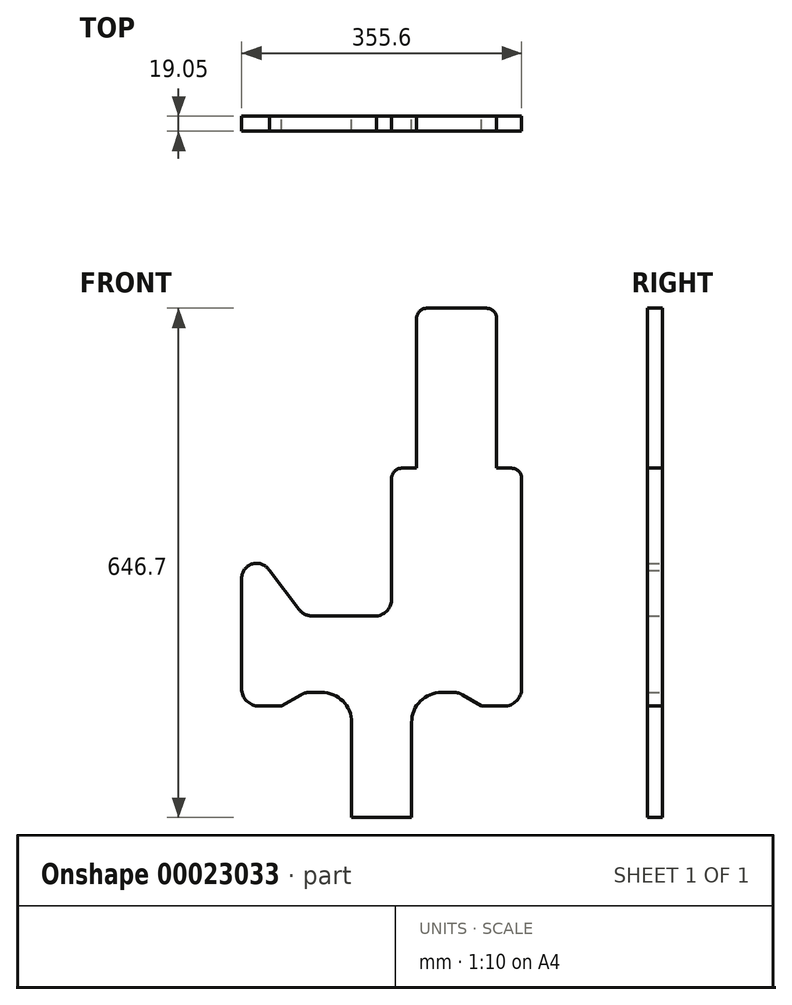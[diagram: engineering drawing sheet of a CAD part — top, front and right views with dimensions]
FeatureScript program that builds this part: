
annotation { "Feature Type Name" : "Feature", "Feature Type Description" : "" }
export const myFeature = defineFeature(function(context is Context, id is Id, definition is map)
    precondition{}
    {
        {
            var Q0;
            Q0=qCreatedBy(makeId("Front.planeOp"),FACE);
            var sketch = newSketch(context, id + "F0", { "sketchPlane" : qUnion([Q0])});
            skLineSegment(sketch, "E0", {"start": v(165.1, -62.38) * mm, "end": v(165.1, 204.91) * mm});
            skLineSegment(sketch, "E1", {"start": v(152.4, 217.61) * mm, "end": v(133.35, 217.61) * mm});
            skLineSegment(sketch, "E2", {"start": v(133.35, 217.61) * mm, "end": v(133.35, 408.11) * mm});
            skLineSegment(sketch, "E3", {"start": v(120.65, 420.81) * mm, "end": v(44.45, 420.81) * mm});
            skLineSegment(sketch, "E4", {"start": v(31.75, 408.11) * mm, "end": v(31.75, 217.61) * mm});
            skLineSegment(sketch, "E5", {"start": v(31.75, 217.61) * mm, "end": v(23.4, 217.61) * mm});
            skLineSegment(sketch, "E6", {"start": v(-190.5, -62.38) * mm, "end": v(-190.5, 29.7) * mm});
            skArc(sketch, "E7.filletArc", {"start": v(133.35, 408.11) * mm, "mid": v(129.63, 417.1) * mm, "end": v(120.65, 420.81) * mm});
            skArc(sketch, "E8.filletArc", {"start": v(44.45, 420.81) * mm, "mid": v(35.47, 417.1) * mm, "end": v(31.75, 408.11) * mm});
            skArc(sketch, "E9.filletArc", {"start": v(165.1, 204.91) * mm, "mid": v(161.38, 213.9) * mm, "end": v(152.4, 217.61) * mm});
            skLineSegment(sketch, "E10", {"start": v(31.75, 217.61) * mm, "end": v(12.7, 217.61) * mm});
            skLineSegment(sketch, "E11", {"start": v(0, 204.91) * mm, "end": v(0, 51.68) * mm});
            skArc(sketch, "E12.filletArc", {"start": v(12.7, 217.61) * mm, "mid": v(3.72, 213.9) * mm, "end": v(0, 204.91) * mm});
            skArc(sketch, "E13.filletArc", {"start": v(142.88, -84.6) * mm, "mid": v(158.6, -78.1) * mm, "end": v(165.1, -62.38) * mm});
            skArc(sketch, "E14.filletArc", {"start": v(-190.5, -62.38) * mm, "mid": v(-184, -78.1) * mm, "end": v(-168.28, -84.6) * mm});
            skLineSegment(sketch, "E15", {"start": v(-100.1, 29.7) * mm, "end": v(-19, 29.7) * mm});
            skLineSegment(sketch, "E16", {"start": v(-190.5, 29.7) * mm, "end": v(-190.5, 77.85) * mm});
            skArc(sketch, "E17.filletArc", {"start": v(-19, 29.7) * mm, "mid": v(-5.4, 37.16) * mm, "end": v(0, 51.68) * mm});
            skArc(sketch, "E18", {"start": v(-155.17, 87.73) * mm, "mid": v(-176.58, 96.2) * mm, "end": v(-190.5, 77.85) * mm});
            skLineSegment(sketch, "E19", {"start": v(-155.17, 87.73) * mm, "end": v(-117.8, 38.48) * mm});
            skArc(sketch, "E20.filletArc", {"start": v(-117.8, 38.48) * mm, "mid": v(-109.98, 32.01) * mm, "end": v(-100.1, 29.7) * mm});
            skLineSegment(sketch, "E21", {"start": v(142.88, -84.6) * mm, "end": v(114.3, -84.6) * mm});
            skLineSegment(sketch, "E22", {"start": v(-168.28, -84.6) * mm, "end": v(-139.7, -84.6) * mm});
            skLineSegment(sketch, "E23", {"start": v(-139.7, -84.6) * mm, "end": v(-115.4, -70.24) * mm});
            skLineSegment(sketch, "E24", {"start": v(90, -70.24) * mm, "end": v(114.3, -84.6) * mm});
            skArc(sketch, "E25.filletArc", {"start": v(-104.1, -67.14) * mm, "mid": v(-109.96, -67.93) * mm, "end": v(-115.4, -70.24) * mm});
            skArc(sketch, "E26.filletArc", {"start": v(90, -70.24) * mm, "mid": v(84.56, -67.93) * mm, "end": v(78.7, -67.14) * mm});
            skLineSegment(sketch, "E27", {"start": v(-12.7, -225.9) * mm, "end": v(25.4, -225.9) * mm});
            skLineSegment(sketch, "E28", {"start": v(-12.7, -225.9) * mm, "end": v(-50.8, -225.9) * mm});
            skLineSegment(sketch, "E29", {"start": v(25.4, -225.9) * mm, "end": v(25.4, -105.24) * mm});
            skLineSegment(sketch, "E30", {"start": v(-50.8, -225.9) * mm, "end": v(-50.8, -105.24) * mm});
            skLineSegment(sketch, "E31", {"start": v(-104.1, -67.14) * mm, "end": v(-88.9, -67.14) * mm});
            skLineSegment(sketch, "E32", {"start": v(63.5, -67.14) * mm, "end": v(78.7, -67.14) * mm});
            skArc(sketch, "E33.filletArc", {"start": v(-50.8, -105.24) * mm, "mid": v(-61.96, -78.3) * mm, "end": v(-88.9, -67.14) * mm});
            skArc(sketch, "E34.filletArc", {"start": v(63.5, -67.14) * mm, "mid": v(36.56, -78.3) * mm, "end": v(25.4, -105.24) * mm});
            skSolve(sketch);
        }
        {
            var Q0;
            Q0=makeQuery(id+"F0.imprint","IMPRINT",FACE,{"disambiguationData":[TD([[makeQuery(id+"F0.imprint","IMPRINT",EDGE,{"derivedFrom":sQuery(id+"F0.wireOp",EDGE,"E0")}),1.0]])]});
            extrude(context, id + "F1", {"entities" : qUnion([Q0]), "depth" : 19.05 * mm});
        }
    });
